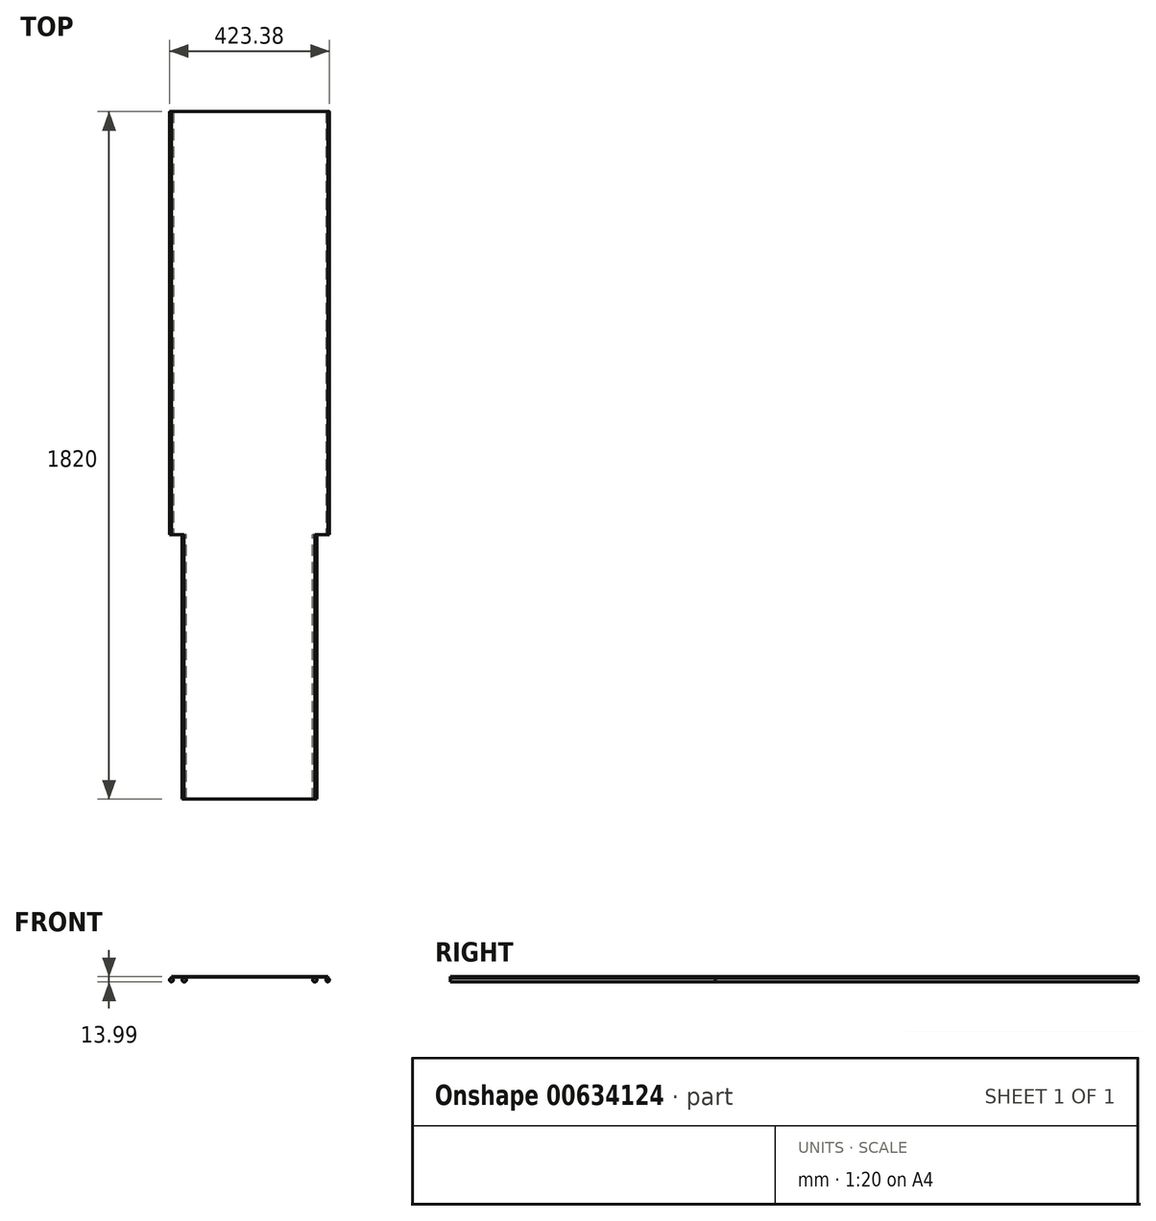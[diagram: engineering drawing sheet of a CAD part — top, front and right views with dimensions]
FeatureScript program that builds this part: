
annotation { "Feature Type Name" : "Feature", "Feature Type Description" : "" }
export const myFeature = defineFeature(function(context is Context, id is Id, definition is map)
    precondition{}
    {
        {
            var Q0;
            Q0=qCreatedBy(makeId("Front.planeOp"),FACE);
            var sketch = newSketch(context, id + "F0", { "sketchPlane" : qUnion([Q0])});
            skLineSegment(sketch, "E0.bottom", {"start": v(-15, 40) * mm, "end": v(15, 40) * mm});
            skLineSegment(sketch, "E0.top", {"start": v(-12, 0) * mm, "end": v(12, 0) * mm});
            skLineSegment(sketch, "E0.left", {"start": v(-15, 40) * mm, "end": v(-15, 37) * mm});
            skLineSegment(sketch, "E0.right", {"start": v(15, 37) * mm, "end": v(15, 3) * mm});
            skLineSegment(sketch, "E1.0", {"start": v(-15, 37) * mm, "end": v(3, 37) * mm});
            skLineSegment(sketch, "E1.1", {"start": v(-12, 6) * mm, "end": v(-12, 6) * mm});
            skLineSegment(sketch, "E1.2", {"start": v(-9, 3) * mm, "end": v(9, 3) * mm});
            skLineSegment(sketch, "E1.3", {"start": v(12, 29.6) * mm, "end": v(12, 6) * mm});
            skLineSegment(sketch, "E2.0", {"start": v(-15, 6) * mm, "end": v(-12, 6) * mm});
            skLineSegment(sketch, "E3", {"start": v(12, 40) * mm, "end": v(7.5, 40) * mm, "construction": true});
            skLineSegment(sketch, "E4", {"start": v(7, 34.8) * mm, "end": v(7, 40) * mm, "construction": true});
            skArc(sketch, "E5", {"start": v(7, 40) * mm, "mid": v(6.75, 29.6) * mm, "end": v(7.5, 39.98) * mm});
            skLineSegment(sketch, "E6.trimOffspring", {"start": v(-15, 6) * mm, "end": v(-15, 3) * mm});
            skPoint(sketch, "E7.orphan", {"position": v(5, 29.7) * mm});
            skPoint(sketch, "E8.visualSharp", {"position": v(15, 40) * mm});
            skArc(sketch, "E8.filletArc", {"start": v(15, 37) * mm, "mid": v(14.12, 39.12) * mm, "end": v(12, 40) * mm});
            skPoint(sketch, "E9.visualSharp", {"position": v(15, 0) * mm});
            skArc(sketch, "E9.filletArc", {"start": v(12, 0) * mm, "mid": v(14.12, 0.88) * mm, "end": v(15, 3) * mm});
            skArc(sketch, "E10.filletArc", {"start": v(9, 3) * mm, "mid": v(11.12, 3.88) * mm, "end": v(12, 6) * mm});
            skPoint(sketch, "E11.visualSharp", {"position": v(-12, 3) * mm});
            skArc(sketch, "E11.filletArc", {"start": v(-12, 6) * mm, "mid": v(-11.12, 3.88) * mm, "end": v(-9, 3) * mm});
            skPoint(sketch, "E12.visualSharp", {"position": v(-15, 0) * mm});
            skArc(sketch, "E12.filletArc", {"start": v(-15, 3) * mm, "mid": v(-14.12, 0.88) * mm, "end": v(-12, 0) * mm});
            skLineSegment(sketch, "E13.0", {"start": v(6.5, 34.8) * mm, "end": v(6.5, 39.8) * mm});
            skLineSegment(sketch, "E14.0", {"start": v(7.5, 34.8) * mm, "end": v(7.5, 40) * mm});
            skLineSegment(sketch, "E15", {"start": v(-15, 6) * mm, "end": v(-15, 16) * mm});
            skLineSegment(sketch, "E16", {"start": v(-15, 16) * mm, "end": v(-12, 16) * mm});
            skLineSegment(sketch, "E17", {"start": v(-12, 16) * mm, "end": v(-12, 6) * mm});
            skLineSegment(sketch, "E18", {"start": v(6.75, 29.6) * mm, "end": v(12, 29.6) * mm});
            skSolve(sketch);
        }
        {
            var Q0;
            Q0=qCreatedBy(makeId("Front.planeOp"),FACE);
            var sketch = newSketch(context, id + "F1", { "sketchPlane" : qUnion([Q0])});
            skLineSegment(sketch, "E19.1.1", {"start": v(7.5, 40) * mm, "end": v(-15, 40) * mm});
            skLineSegment(sketch, "E19.1.2", {"start": v(-15, 40) * mm, "end": v(-15, 37) * mm});
            skArc(sketch, "E19.2.8", {"start": v(-15, 3) * mm, "mid": v(-14.12, 0.88) * mm, "end": v(-12, 0) * mm, "construction": true});
            skLineSegment(sketch, "E19.2.9", {"start": v(-12, 0) * mm, "end": v(-5, 0) * mm});
            skLineSegment(sketch, "E19.2.13", {"start": v(17, 40) * mm, "end": v(8.5, 40) * mm});
            skLineSegment(sketch, "E19.3.0", {"start": v(-15, 18) * mm, "end": v(-15, 7.7) * mm});
            skPoint(sketch, "E20.2", {"position": v(6.5, 37.3) * mm});
            skPoint(sketch, "E21.orphan", {"position": v(6.5, 39.8) * mm});
            skPoint(sketch, "E19.0.2.end.orphan", {"position": v(7, 40) * mm});
            skPoint(sketch, "E22.orphan", {"position": v(12, 29.6) * mm});
            skPoint(sketch, "E23.orphan", {"position": v(7.5, 34.8) * mm});
            skPoint(sketch, "E20.0.start.orphan", {"position": v(6.5, 34.8) * mm});
            skLineSegment(sketch, "E24", {"start": v(-15, 37) * mm, "end": v(-15, 31) * mm});
            skLineSegment(sketch, "E25", {"start": v(0, 0) * mm, "end": v(0, 15) * mm, "construction": true});
            skLineSegment(sketch, "E26", {"start": v(7.5, 40) * mm, "end": v(7.5, 37.97) * mm});
            skLineSegment(sketch, "E27", {"start": v(8.5, 40) * mm, "end": v(8.5, 37.97) * mm});
            skLineSegment(sketch, "E28", {"start": v(15, 32.5) * mm, "end": v(8, 32.5) * mm, "construction": true});
            skPoint(sketch, "E29.orphan", {"position": v(7.6, 39) * mm});
            skLineSegment(sketch, "E30", {"start": v(8, 39) * mm, "end": v(8, 32.5) * mm, "construction": true});
            skPoint(sketch, "E19.3.3.end.orphan", {"position": v(-15, 16) * mm});
            skPoint(sketch, "E19.3.3.start.orphan", {"position": v(-12, 16) * mm});
            skLineSegment(sketch, "E31", {"start": v(-15, 3) * mm, "end": v(-15, 0) * mm});
            skLineSegment(sketch, "E32", {"start": v(-12, 0) * mm, "end": v(-15, 0) * mm});
            skLineSegment(sketch, "E33", {"start": v(-15, 40) * mm, "end": v(-15, 31) * mm, "construction": true});
            skLineSegment(sketch, "E34", {"start": v(-15, 40) * mm, "end": v(-15, 31) * mm});
            skLineSegment(sketch, "E35.trimOffspring", {"start": v(-15, 31) * mm, "end": v(-15, 26) * mm});
            skLineSegment(sketch, "E36.trimOffspring", {"start": v(-15, 29) * mm, "end": v(-15, 24) * mm});
            skPoint(sketch, "E37.orphan", {"position": v(12, 40) * mm});
            skPoint(sketch, "E38.orphan", {"position": v(12, 0) * mm});
            skLineSegment(sketch, "E39.0", {"start": v(13.1, 38) * mm, "end": v(13.1, 38) * mm});
            skLineSegment(sketch, "E40.1", {"start": v(-13, 2) * mm, "end": v(-11, 2) * mm, "construction": true});
            skLineSegment(sketch, "E41.0", {"start": v(-13, 38) * mm, "end": v(-13, 34) * mm});
            skArc(sketch, "E42", {"start": v(13.32, 33.87) * mm, "mid": v(11.56, 36.69) * mm, "end": v(8.5, 37.97) * mm});
            skLineSegment(sketch, "E43.0", {"start": v(29.42, 20) * mm, "end": v(-7, 20) * mm, "construction": true});
            skLineSegment(sketch, "E44.trimOffspring", {"start": v(-13, 0.17) * mm, "end": v(-13, 0) * mm});
            skArc(sketch, "E45.0", {"start": v(2.9, 38) * mm, "mid": v(3.81, 26.3) * mm, "end": v(15, 29.84) * mm});
            skLineSegment(sketch, "E46.trimOffspring", {"start": v(2.9, 38) * mm, "end": v(-13, 38) * mm});
            skLineSegment(sketch, "E47.trimOffspring", {"start": v(13.32, 33.87) * mm, "end": v(13.43, 31.7) * mm});
            skArc(sketch, "E48.trimOffspring", {"start": v(13.1, 38) * mm, "mid": v(13.1, 38) * mm, "end": v(13.1, 38) * mm});
            skArc(sketch, "E49.trimOffspring", {"start": v(7.5, 37.97) * mm, "mid": v(4.01, 28.73) * mm, "end": v(13.43, 31.7) * mm});
            skPoint(sketch, "E50.orphan", {"position": v(7.5, 39) * mm});
            skPoint(sketch, "E51.start.orphan", {"position": v(8.5, 39) * mm});
            skLineSegment(sketch, "E52.0", {"start": v(8, 0) * mm, "end": v(8, 13.5) * mm});
            skLineSegment(sketch, "E53.0", {"start": v(-5, 0) * mm, "end": v(-5, 13.5) * mm});
            skLineSegment(sketch, "E54.0", {"start": v(16.47, 12) * mm, "end": v(14.46, 12) * mm, "construction": true});
            skLineSegment(sketch, "E55.trimOffspring", {"start": v(12.84, 12) * mm, "end": v(10, 12) * mm});
            skLineSegment(sketch, "E56.0", {"start": v(1.5, 0) * mm, "end": v(1.5, 20) * mm, "construction": true});
            skLineSegment(sketch, "E57", {"start": v(1.5, 20) * mm, "end": v(-9.16, 15.5) * mm});
            skLineSegment(sketch, "E58", {"start": v(1.5, 20) * mm, "end": v(10.84, 15.5) * mm});
            skLineSegment(sketch, "E59.0", {"start": v(-9.16, 13.5) * mm, "end": v(-5, 13.5) * mm});
            skLineSegment(sketch, "E60", {"start": v(-9.16, 15.5) * mm, "end": v(-9.16, 13.5) * mm});
            skLineSegment(sketch, "E61", {"start": v(10.84, 15.5) * mm, "end": v(10.84, 13.5) * mm});
            skLineSegment(sketch, "E62.trimOffspring", {"start": v(8, 13.5) * mm, "end": v(10.84, 13.5) * mm});
            skLineSegment(sketch, "E63.trimOffspring", {"start": v(10, 2) * mm, "end": v(15, 2) * mm});
            skLineSegment(sketch, "E64.trimOffspring", {"start": v(8, 0) * mm, "end": v(17, 0) * mm});
            skLineSegment(sketch, "E65.0", {"start": v(10, 2) * mm, "end": v(10, 12) * mm});
            skLineSegment(sketch, "E66.0", {"start": v(1.55, 22.2) * mm, "end": v(-7, 18.58) * mm});
            skLineSegment(sketch, "E66.1", {"start": v(1.55, 22.2) * mm, "end": v(12.84, 16.75) * mm});
            skLineSegment(sketch, "E67.0", {"start": v(-11.16, 16.82) * mm, "end": v(-11.16, 15.5) * mm});
            skLineSegment(sketch, "E68.0", {"start": v(-13, 11.5) * mm, "end": v(-7, 11.5) * mm});
            skLineSegment(sketch, "E69", {"start": v(-11.16, 15.5) * mm, "end": v(-11.16, 13.5) * mm});
            skLineSegment(sketch, "E70.0", {"start": v(12.84, 16.75) * mm, "end": v(12.84, 12) * mm});
            skLineSegment(sketch, "E71.0", {"start": v(-13, 6.7) * mm, "end": v(-7, 6.7) * mm, "construction": true});
            skLineSegment(sketch, "E72.0", {"start": v(-15, 7.7) * mm, "end": v(-13, 7.7) * mm});
            skLineSegment(sketch, "E73.0", {"start": v(-15, 5.7) * mm, "end": v(-11, 5.7) * mm});
            skLineSegment(sketch, "E74.0", {"start": v(-15, 3.7) * mm, "end": v(-13, 3.7) * mm, "construction": true});
            skLineSegment(sketch, "E75.trimOffspring", {"start": v(-15, 5.7) * mm, "end": v(-15, 3) * mm});
            skLineSegment(sketch, "E76.trimOffspring", {"start": v(-13, 3.7) * mm, "end": v(-13, 2) * mm, "construction": true});
            skLineSegment(sketch, "E77.trimOffspring", {"start": v(-11, 5.7) * mm, "end": v(-11, 2) * mm});
            skLineSegment(sketch, "E78.0", {"start": v(-13, 13.5) * mm, "end": v(-11.16, 13.5) * mm});
            skLineSegment(sketch, "E79.trimOffspring", {"start": v(-9.16, 13.5) * mm, "end": v(-7, 13.5) * mm});
            skLineSegment(sketch, "E80.trimOffspring", {"start": v(-13, 11.5) * mm, "end": v(-13, 7.7) * mm});
            skLineSegment(sketch, "E81.0", {"start": v(-7, 11.5) * mm, "end": v(-7, 3.7) * mm});
            skLineSegment(sketch, "E82.trimOffspring", {"start": v(-11, 3.7) * mm, "end": v(-7, 3.7) * mm});
            skLineSegment(sketch, "E83.0", {"start": v(17, 40) * mm, "end": v(17, 0) * mm});
            skPoint(sketch, "E84.orphan", {"position": v(17.1, 0) * mm});
            skLineSegment(sketch, "E85.trimOffspring", {"start": v(15, 29.84) * mm, "end": v(15, 2) * mm});
            skPoint(sketch, "E86.start.orphan", {"position": v(15, 40) * mm});
            skLineSegment(sketch, "E87", {"start": v(-13, 13.5) * mm, "end": v(-13, 18) * mm});
            skLineSegment(sketch, "E88.trimOffspring", {"start": v(-15, 22) * mm, "end": v(-15, 21.16) * mm, "construction": true});
            skLineSegment(sketch, "E89.trimOffspring", {"start": v(-15, 22) * mm, "end": v(-15, 18) * mm});
            skPoint(sketch, "E90.start.orphan", {"position": v(-12, 28) * mm});
            skPoint(sketch, "E91.orphan", {"position": v(-12, 29) * mm});
            skLineSegment(sketch, "E92.0", {"start": v(-9, 26) * mm, "end": v(-11, 26) * mm});
            skLineSegment(sketch, "E93.0", {"start": v(-11, 24) * mm, "end": v(-13, 24) * mm});
            skLineSegment(sketch, "E94", {"start": v(-9, 20) * mm, "end": v(-9, 26) * mm});
            skLineSegment(sketch, "E95.0", {"start": v(-11, 20) * mm, "end": v(-11, 22) * mm});
            skLineSegment(sketch, "E96.trimOffspring", {"start": v(-11, 24) * mm, "end": v(-11, 26) * mm});
            skLineSegment(sketch, "E97.trimOffspring", {"start": v(-13, 28) * mm, "end": v(-13, 34) * mm});
            skLineSegment(sketch, "E98", {"start": v(-15, 22) * mm, "end": v(-11, 22) * mm});
            skLineSegment(sketch, "E99", {"start": v(-13, 24) * mm, "end": v(-15, 24) * mm});
            skLineSegment(sketch, "E100.0", {"start": v(-7, 18.58) * mm, "end": v(-7, 28) * mm});
            skLineSegment(sketch, "E101.0", {"start": v(-13, 18) * mm, "end": v(-8.36, 18) * mm});
            skLineSegment(sketch, "E102.trimOffspring", {"start": v(-8.36, 18) * mm, "end": v(-11.16, 16.82) * mm});
            skLineSegment(sketch, "E103.0", {"start": v(-11, 20) * mm, "end": v(-9, 20) * mm});
            skLineSegment(sketch, "E104.0", {"start": v(-7, 28) * mm, "end": v(-13, 28) * mm});
            skSolve(sketch);
        }
        {
            var Q0;
            Q0=qSketchRegion(id+"F1",true);
            extrude(context, id + "F2", {"entities" : qUnion([Q0]), "oppositeDirection" : true, "depth" : 1910 * mm, "offsetDistance" : 25 * mm});
        }
        {
            var Q0;
            Q0=makeQuery(id+"F1.imprint","IMPRINT",FACE,{"disambiguationData":[TD([[makeQuery(id+"F1.imprint","IMPRINT",EDGE,{"derivedFrom":sQuery(id+"F1.wireOp",EDGE,"E19.1.1")}),1.0]])]});
            var sketch = newSketch(context, id + "F3", { "sketchPlane" : qUnion([Q0])});
            skLineSegment(sketch, "E105.0", {"start": v(-13.5, 18) * mm, "end": v(-13.5, -0.51) * mm});
            skSolve(sketch);
        }
        {
            var Q0;
            Q0=makeQuery(id+"F3.imprint","IMPRINT",FACE,{"disambiguationData":[TD([[makeQuery(id+"F3.imprint","IMPRINT",EDGE,{"derivedFrom":makeQuery(id+"F1.imprint","IMPRINT",EDGE,{"derivedFrom":sQuery(id+"F1.wireOp",EDGE,"E19.1.1")})}),1.0]])]});
            var sketch = newSketch(context, id + "F4", { "sketchPlane" : qUnion([Q0])});
            skLineSegment(sketch, "E106.0", {"start": v(-17, 40) * mm, "end": v(-25.5, 40) * mm});
            skLineSegment(sketch, "E107.0", {"start": v(-49.1, 40) * mm, "end": v(-49.1, 18) * mm});
            skLineSegment(sketch, "E108.0", {"start": v(-17, 40) * mm, "end": v(-17, 18) * mm});
            skPoint(sketch, "E109.orphan", {"position": v(7.5, 40) * mm});
            skLineSegment(sketch, "E110.1", {"start": v(-19, 29.83) * mm, "end": v(-19, 20) * mm});
            skLineSegment(sketch, "E110.3", {"start": v(-47.1, 38) * mm, "end": v(-47.1, 20) * mm});
            skArc(sketch, "E111.0", {"start": v(7.5, 37.97) * mm, "mid": v(4.01, 28.73) * mm, "end": v(13.43, 31.7) * mm, "construction": true});
            skLineSegment(sketch, "E112.0", {"start": v(17, 40) * mm, "end": v(8.5, 40) * mm});
            skLineSegment(sketch, "E113.0", {"start": v(7.5, 40) * mm, "end": v(-15, 40) * mm});
            skLineSegment(sketch, "E114.0", {"start": v(-26.6, 40) * mm, "end": v(-26.6, 37.97) * mm});
            skLineSegment(sketch, "E115.0", {"start": v(-25.5, 40) * mm, "end": v(-25.5, 37.98) * mm});
            skLineSegment(sketch, "E116.0", {"start": v(-7, 18.58) * mm, "end": v(-7, 28) * mm});
            skLineSegment(sketch, "E117", {"start": v(-47.1, 23.29) * mm, "end": v(15, 23.29) * mm, "construction": true});
            skPoint(sketch, "E118.orphan", {"position": v(-7, 23.29) * mm});
            skLineSegment(sketch, "E119", {"start": v(8, 32.5) * mm, "end": v(2.5, 32.5) * mm});
            skLineSegment(sketch, "E120.0", {"start": v(8, 39) * mm, "end": v(8, 32.5) * mm});
            skLineSegment(sketch, "E120.1", {"start": v(17, 40) * mm, "end": v(17, 0) * mm});
            skLineSegment(sketch, "E121.trimOffspring", {"start": v(-17, 32.5) * mm, "end": v(-26, 32.5) * mm, "construction": true});
            skArc(sketch, "E122", {"start": v(-26.6, 37.97) * mm, "mid": v(-25.95, 27.01) * mm, "end": v(-25.5, 37.98) * mm});
            skArc(sketch, "E123.0", {"start": v(-31.1, 38) * mm, "mid": v(-30.2, 26.3) * mm, "end": v(-19, 29.83) * mm});
            skLineSegment(sketch, "E124.trimOffspring", {"start": v(-26.6, 40) * mm, "end": v(-49.1, 40) * mm});
            skLineSegment(sketch, "E125.trimOffspring", {"start": v(-26.6, 27.05) * mm, "end": v(-26.6, 20) * mm, "construction": true});
            skLineSegment(sketch, "E126.trimOffspring", {"start": v(-25.5, 27.04) * mm, "end": v(-25.5, 20) * mm, "construction": true});
            skLineSegment(sketch, "E127.trimOffspring", {"start": v(-31.1, 38) * mm, "end": v(-47.1, 38) * mm});
            skLineSegment(sketch, "E128.0", {"start": v(-49.1, 18) * mm, "end": v(-17, 18) * mm});
            skPoint(sketch, "E129.orphan", {"position": v(-8.36, 18) * mm});
            skPoint(sketch, "E130.orphan", {"position": v(-13, 18) * mm});
            skLineSegment(sketch, "E131.0", {"start": v(-47.1, 20) * mm, "end": v(-19, 20) * mm});
            skSolve(sketch);
        }
        {
            var Q0;
            Q0=makeQuery(id+"F1.imprint","IMPRINT",FACE,{"disambiguationData":[TD([[makeQuery(id+"F1.imprint","IMPRINT",EDGE,{"derivedFrom":sQuery(id+"F1.wireOp",EDGE,"E19.1.1")}),1.0]])]});
            var sketch = newSketch(context, id + "F5", { "sketchPlane" : qUnion([Q0])});
            skArc(sketch, "E132.0", {"start": v(7.5, 37.97) * mm, "mid": v(4.01, 28.73) * mm, "end": v(13.43, 31.7) * mm, "construction": true});
            skArc(sketch, "E132.1", {"start": v(13.32, 33.87) * mm, "mid": v(11.56, 36.69) * mm, "end": v(8.5, 37.97) * mm, "construction": true});
            skLineSegment(sketch, "E132.2", {"start": v(7.5, 40) * mm, "end": v(-15, 40) * mm});
            skArc(sketch, "E132.3", {"start": v(-26.6, 37.97) * mm, "mid": v(-25.95, 27.01) * mm, "end": v(-25.5, 37.98) * mm, "construction": true});
            skLineSegment(sketch, "E133.0", {"start": v(-15, 40) * mm, "end": v(-25.5, 40) * mm});
            skPoint(sketch, "E134.orphan", {"position": v(-26.6, 40) * mm});
            skLineSegment(sketch, "E135.0", {"start": v(7.5, 40) * mm, "end": v(7.5, 37.37) * mm});
            skLineSegment(sketch, "E135.1", {"start": v(8.5, 40) * mm, "end": v(8.5, 37.37) * mm});
            skLineSegment(sketch, "E135.2", {"start": v(-25.5, 40) * mm, "end": v(-25.5, 37.37) * mm});
            skLineSegment(sketch, "E135.3", {"start": v(-26.6, 40) * mm, "end": v(-26.6, 37.36) * mm});
            skPoint(sketch, "E135.4", {"position": v(-25.5, 38.99) * mm});
            skLineSegment(sketch, "E136", {"start": v(-49.1, 40) * mm, "end": v(-198.8, 40) * mm});
            skLineSegment(sketch, "E137.0", {"start": v(8.5, 41) * mm, "end": v(-198.8, 41) * mm});
            skLineSegment(sketch, "E138", {"start": v(8.5, 40) * mm, "end": v(8.5, 41) * mm});
            skLineSegment(sketch, "E139", {"start": v(-198.8, 41) * mm, "end": v(-198.8, 40) * mm, "construction": true});
            skArc(sketch, "E140.0", {"start": v(7.5, 37.37) * mm, "mid": v(4.47, 29.12) * mm, "end": v(12.84, 31.8) * mm});
            skArc(sketch, "E141.0", {"start": v(12.74, 33.72) * mm, "mid": v(11.2, 36.21) * mm, "end": v(8.5, 37.37) * mm});
            skArc(sketch, "E142", {"start": v(12.74, 33.72) * mm, "mid": v(12.88, 32.76) * mm, "end": v(12.84, 31.8) * mm});
            skPoint(sketch, "E143.orphan", {"position": v(7.5, 37.97) * mm});
            skPoint(sketch, "E144.orphan", {"position": v(8.5, 37.97) * mm});
            skArc(sketch, "E145.0", {"start": v(-26.6, 37.36) * mm, "mid": v(-25.95, 27.61) * mm, "end": v(-25.5, 37.37) * mm});
            skPoint(sketch, "E146.orphan", {"position": v(-26.6, 37.97) * mm});
            skPoint(sketch, "E147.orphan", {"position": v(-25.5, 37.98) * mm});
            skLineSegment(sketch, "E148.trimOffspring", {"start": v(-26.6, 40) * mm, "end": v(-49.1, 40) * mm});
            skSolve(sketch);
        }
        {
            var Q0;
            Q0=qCreatedBy(makeId("Front.planeOp"),FACE);
            var sketch = newSketch(context, id + "F6", { "sketchPlane" : qUnion([Q0])});
            skLineSegment(sketch, "E149.3", {"start": v(8.5, 40) * mm, "end": v(8.5, 37.37) * mm});
            skLineSegment(sketch, "E149.4", {"start": v(7.5, 40) * mm, "end": v(7.5, 37.37) * mm});
            skLineSegment(sketch, "E149.5", {"start": v(7.5, 40) * mm, "end": v(-15, 40) * mm});
            skLineSegment(sketch, "E149.6", {"start": v(8.5, 41) * mm, "end": v(-198.8, 41) * mm});
            skLineSegment(sketch, "E149.7", {"start": v(8.5, 40) * mm, "end": v(8.5, 41) * mm});
            skLineSegment(sketch, "E149.8", {"start": v(-25.5, 40) * mm, "end": v(-198.8, 40) * mm});
            skLineSegment(sketch, "E149.9", {"start": v(-198.8, 41) * mm, "end": v(-198.8, 40) * mm});
            skLineSegment(sketch, "E150.0", {"start": v(-15, 40) * mm, "end": v(-25.5, 40) * mm});
            skLineSegment(sketch, "E151.0", {"start": v(8, 32.5) * mm, "end": v(2.5, 32.5) * mm, "construction": true});
            skLineSegment(sketch, "E151.1", {"start": v(8, 39) * mm, "end": v(8, 32.5) * mm, "construction": true});
            skArc(sketch, "E152", {"start": v(7.5, 37.37) * mm, "mid": v(8, 27.62) * mm, "end": v(8.5, 37.37) * mm});
            skPoint(sketch, "E153.orphan", {"position": v(-49.1, 40) * mm});
            skSolve(sketch);
        }
        {
            var Q0;
            Q0 = qSketchRegion(id + "F6", true);
            extrude(context, id + "F7", {"entities" : qUnion([Q0]), "operationType" : NewBodyOperationType.ADD, "oppositeDirection" : true, "depth" : 1120 * mm, "offsetDistance" : 25 * mm});
        }
        {
            var Q0;
            {var subQ7=sQuery(id+"F5.wireOp",EDGE,"E132.2");Q0=makeQuery(id+"F5.imprint","IMPRINT",FACE,{"disambiguationData":[TD([[makeQuery(id+"F5.imprint","IMPRINT",EDGE,{"derivedFrom":subQ7}),1.0]])]});}
            var sketch = newSketch(context, id + "F8", { "sketchPlane" : qUnion([Q0])});
            skLineSegment(sketch, "E154.0.0", {"start": v(-15, 0) * mm, "end": v(-13, 0) * mm});
            skLineSegment(sketch, "E154.0.1", {"start": v(-13, 0) * mm, "end": v(-12, 0) * mm});
            skLineSegment(sketch, "E154.0.2", {"start": v(-12, 0) * mm, "end": v(-5, 0) * mm});
            skLineSegment(sketch, "E154.0.3", {"start": v(-5, 0) * mm, "end": v(-5, 13.5) * mm});
            skLineSegment(sketch, "E154.0.4", {"start": v(-5, 13.5) * mm, "end": v(-7, 13.5) * mm});
            skLineSegment(sketch, "E154.0.5", {"start": v(-7, 13.5) * mm, "end": v(-9.16, 13.5) * mm});
            skLineSegment(sketch, "E154.0.6", {"start": v(-9.16, 13.5) * mm, "end": v(-9.16, 15.5) * mm});
            skLineSegment(sketch, "E154.0.7", {"start": v(-9.16, 15.5) * mm, "end": v(1.5, 20) * mm});
            skLineSegment(sketch, "E154.0.8", {"start": v(1.5, 20) * mm, "end": v(10.84, 15.5) * mm});
            skLineSegment(sketch, "E154.0.9", {"start": v(10.84, 15.5) * mm, "end": v(10.84, 13.5) * mm});
            skLineSegment(sketch, "E154.0.10", {"start": v(10.84, 13.5) * mm, "end": v(8, 13.5) * mm});
            skLineSegment(sketch, "E154.0.11", {"start": v(8, 13.5) * mm, "end": v(8, 0) * mm});
            skLineSegment(sketch, "E154.0.12", {"start": v(8, 0) * mm, "end": v(17, 0) * mm});
            skLineSegment(sketch, "E154.0.13", {"start": v(17, 0) * mm, "end": v(17, 40) * mm});
            skLineSegment(sketch, "E154.0.14", {"start": v(17, 40) * mm, "end": v(8.5, 40) * mm});
            skLineSegment(sketch, "E154.0.15", {"start": v(8.5, 40) * mm, "end": v(8.5, 37.97) * mm});
            skArc(sketch, "E154.0.16", {"start": v(8.5, 37.97) * mm, "mid": v(11.56, 36.69) * mm, "end": v(13.32, 33.87) * mm});
            skLineSegment(sketch, "E154.0.17", {"start": v(13.32, 33.87) * mm, "end": v(13.43, 31.7) * mm});
            skArc(sketch, "E154.0.18", {"start": v(13.43, 31.7) * mm, "mid": v(4.01, 28.73) * mm, "end": v(7.5, 37.97) * mm});
            skLineSegment(sketch, "E154.0.19", {"start": v(7.5, 37.97) * mm, "end": v(7.5, 40) * mm});
            skLineSegment(sketch, "E154.0.20", {"start": v(7.5, 40) * mm, "end": v(-15, 40) * mm});
            skLineSegment(sketch, "E154.0.21", {"start": v(-15, 40) * mm, "end": v(-15, 31) * mm});
            skLineSegment(sketch, "E154.0.22", {"start": v(-15, 31) * mm, "end": v(-15, 29) * mm});
            skLineSegment(sketch, "E154.0.23", {"start": v(-15, 29) * mm, "end": v(-15, 24) * mm});
            skLineSegment(sketch, "E154.0.24", {"start": v(-15, 24) * mm, "end": v(-13, 24) * mm});
            skLineSegment(sketch, "E154.0.25", {"start": v(-13, 24) * mm, "end": v(-11, 24) * mm});
            skLineSegment(sketch, "E154.0.26", {"start": v(-11, 24) * mm, "end": v(-11, 26) * mm});
            skLineSegment(sketch, "E154.0.27", {"start": v(-11, 26) * mm, "end": v(-9, 26) * mm});
            skLineSegment(sketch, "E154.0.28", {"start": v(-9, 26) * mm, "end": v(-9, 20) * mm});
            skLineSegment(sketch, "E154.0.29", {"start": v(-9, 20) * mm, "end": v(-11, 20) * mm});
            skLineSegment(sketch, "E154.0.30", {"start": v(-11, 20) * mm, "end": v(-11, 22) * mm});
            skLineSegment(sketch, "E154.0.31", {"start": v(-11, 22) * mm, "end": v(-15, 22) * mm});
            skLineSegment(sketch, "E154.0.32", {"start": v(-15, 22) * mm, "end": v(-15, 18) * mm});
            skLineSegment(sketch, "E154.0.33", {"start": v(-15, 18) * mm, "end": v(-15, 7.7) * mm});
            skLineSegment(sketch, "E154.0.34", {"start": v(-15, 7.7) * mm, "end": v(-13, 7.7) * mm});
            skLineSegment(sketch, "E154.0.35", {"start": v(-13, 7.7) * mm, "end": v(-13, 11.5) * mm});
            skLineSegment(sketch, "E154.0.36", {"start": v(-13, 11.5) * mm, "end": v(-7, 11.5) * mm});
            skLineSegment(sketch, "E154.0.37", {"start": v(-7, 11.5) * mm, "end": v(-7, 3.7) * mm});
            skLineSegment(sketch, "E154.0.38", {"start": v(-7, 3.7) * mm, "end": v(-11, 3.7) * mm});
            skLineSegment(sketch, "E154.0.39", {"start": v(-11, 3.7) * mm, "end": v(-11, 5.7) * mm});
            skLineSegment(sketch, "E154.0.40", {"start": v(-11, 5.7) * mm, "end": v(-15, 5.7) * mm});
            skLineSegment(sketch, "E154.0.41", {"start": v(-15, 5.7) * mm, "end": v(-15, 3) * mm});
            skLineSegment(sketch, "E154.0.42", {"start": v(-15, 3) * mm, "end": v(-15, 0) * mm});
            skLineSegment(sketch, "E155.0.0", {"start": v(12.84, 16.75) * mm, "end": v(12.84, 12) * mm});
            skLineSegment(sketch, "E155.0.1", {"start": v(12.84, 12) * mm, "end": v(10, 12) * mm});
            skLineSegment(sketch, "E155.0.2", {"start": v(10, 12) * mm, "end": v(10, 2) * mm});
            skLineSegment(sketch, "E155.0.3", {"start": v(10, 2) * mm, "end": v(15, 2) * mm});
            skLineSegment(sketch, "E155.0.4", {"start": v(15, 2) * mm, "end": v(15, 29.84) * mm});
            skArc(sketch, "E155.0.5", {"start": v(15, 29.84) * mm, "mid": v(3.81, 26.3) * mm, "end": v(2.9, 38) * mm});
            skLineSegment(sketch, "E155.0.6", {"start": v(2.9, 38) * mm, "end": v(-13, 38) * mm});
            skLineSegment(sketch, "E155.0.7", {"start": v(-13, 38) * mm, "end": v(-13, 34) * mm});
            skLineSegment(sketch, "E155.0.8", {"start": v(-13, 34) * mm, "end": v(-13, 28) * mm});
            skLineSegment(sketch, "E155.0.9", {"start": v(-13, 28) * mm, "end": v(-7, 28) * mm});
            skLineSegment(sketch, "E155.0.10", {"start": v(-7, 28) * mm, "end": v(-7, 18.58) * mm});
            skLineSegment(sketch, "E155.0.11", {"start": v(-7, 18.58) * mm, "end": v(1.55, 22.2) * mm});
            skLineSegment(sketch, "E155.0.12", {"start": v(1.55, 22.2) * mm, "end": v(12.84, 16.75) * mm});
            skLineSegment(sketch, "E156.0.0", {"start": v(-8.36, 18) * mm, "end": v(-13, 18) * mm});
            skLineSegment(sketch, "E156.0.1", {"start": v(-13, 18) * mm, "end": v(-13, 13.5) * mm});
            skLineSegment(sketch, "E156.0.2", {"start": v(-13, 13.5) * mm, "end": v(-11.16, 13.5) * mm});
            skLineSegment(sketch, "E156.0.3", {"start": v(-11.16, 13.5) * mm, "end": v(-11.16, 15.5) * mm});
            skLineSegment(sketch, "E156.0.4", {"start": v(-11.16, 15.5) * mm, "end": v(-11.16, 16.82) * mm});
            skLineSegment(sketch, "E156.0.5", {"start": v(-11.16, 16.82) * mm, "end": v(-8.36, 18) * mm});
            skSolve(sketch);
        }
        {
            var Q0;
            Q0 = qSketchRegion(id + "F8", true);
            extrude(context, id + "F9", {"entities" : qUnion([Q0]), "operationType" : NewBodyOperationType.REMOVE, "oppositeDirection" : true, "depth" : 2000 * mm, "offsetDistance" : 25 * mm});
        }
        {
            var Q0;
            Q0=makeQuery(id+"F7.boolean.opBoolean","MERGE",FACE,{"derivedFrom":[makeQuery(id+"F2.opExtrude","CAP_FACE",FACE,{"disambiguationData":[OSD([sQuery(id+"F1.wireOp",EDGE,"E19.1.1"),sQuery(id+"F1.wireOp",EDGE,"E19.2.9"),sQuery(id+"F1.wireOp",EDGE,"E19.2.13"),sQuery(id+"F1.wireOp",EDGE,"E19.3.0"),sQuery(id+"F1.wireOp",EDGE,"E26"),sQuery(id+"F1.wireOp",EDGE,"E27"),sQuery(id+"F1.wireOp",EDGE,"E31"),sQuery(id+"F1.wireOp",EDGE,"E32"),sQuery(id+"F1.wireOp",EDGE,"E34"),sQuery(id+"F1.wireOp",EDGE,"E35.trimOffspring"),sQuery(id+"F1.wireOp",EDGE,"E36.trimOffspring"),sQuery(id+"F1.wireOp",EDGE,"E39.0"),sQuery(id+"F1.wireOp",EDGE,"E39.0"),sQuery(id+"F1.wireOp",EDGE,"E41.0"),sQuery(id+"F1.wireOp",EDGE,"E42"),sQuery(id+"F1.wireOp",EDGE,"E45.0"),sQuery(id+"F1.wireOp",EDGE,"E46.trimOffspring"),sQuery(id+"F1.wireOp",EDGE,"E47.trimOffspring"),sQuery(id+"F1.wireOp",EDGE,"E48.trimOffspring"),sQuery(id+"F1.wireOp",EDGE,"E49.trimOffspring"),sQuery(id+"F1.wireOp",EDGE,"E52.0"),sQuery(id+"F1.wireOp",EDGE,"E53.0"),sQuery(id+"F1.wireOp",EDGE,"E55.trimOffspring"),sQuery(id+"F1.wireOp",EDGE,"E57"),sQuery(id+"F1.wireOp",EDGE,"E58"),sQuery(id+"F1.wireOp",EDGE,"E59.0"),sQuery(id+"F1.wireOp",EDGE,"E60"),sQuery(id+"F1.wireOp",EDGE,"E61"),sQuery(id+"F1.wireOp",EDGE,"E62.trimOffspring"),sQuery(id+"F1.wireOp",EDGE,"E63.trimOffspring"),sQuery(id+"F1.wireOp",EDGE,"E64.trimOffspring"),sQuery(id+"F1.wireOp",EDGE,"E65.0"),sQuery(id+"F1.wireOp",EDGE,"E66.0"),sQuery(id+"F1.wireOp",EDGE,"E66.1"),sQuery(id+"F1.wireOp",EDGE,"E67.0"),sQuery(id+"F1.wireOp",EDGE,"E68.0"),sQuery(id+"F1.wireOp",EDGE,"E69"),sQuery(id+"F1.wireOp",EDGE,"E70.0"),sQuery(id+"F1.wireOp",EDGE,"E72.0"),sQuery(id+"F1.wireOp",EDGE,"E73.0"),sQuery(id+"F1.wireOp",EDGE,"E75.trimOffspring"),sQuery(id+"F1.wireOp",EDGE,"E77.trimOffspring"),sQuery(id+"F1.wireOp",EDGE,"E78.0"),sQuery(id+"F1.wireOp",EDGE,"E79.trimOffspring"),sQuery(id+"F1.wireOp",EDGE,"E80.trimOffspring"),sQuery(id+"F1.wireOp",EDGE,"E81.0"),sQuery(id+"F1.wireOp",EDGE,"E82.trimOffspring"),sQuery(id+"F1.wireOp",EDGE,"E83.0"),sQuery(id+"F1.wireOp",EDGE,"E85.trimOffspring"),sQuery(id+"F1.wireOp",EDGE,"E87"),sQuery(id+"F1.wireOp",EDGE,"E89.trimOffspring"),sQuery(id+"F1.wireOp",EDGE,"E92.0"),sQuery(id+"F1.wireOp",EDGE,"E93.0"),sQuery(id+"F1.wireOp",EDGE,"E94"),sQuery(id+"F1.wireOp",EDGE,"E95.0"),sQuery(id+"F1.wireOp",EDGE,"E96.trimOffspring"),sQuery(id+"F1.wireOp",EDGE,"E97.trimOffspring"),sQuery(id+"F1.wireOp",EDGE,"E98"),sQuery(id+"F1.wireOp",EDGE,"E99"),sQuery(id+"F1.wireOp",EDGE,"E100.0"),sQuery(id+"F1.wireOp",EDGE,"E101.0"),sQuery(id+"F1.wireOp",EDGE,"E102.trimOffspring"),sQuery(id+"F1.wireOp",EDGE,"E103.0"),sQuery(id+"F1.wireOp",EDGE,"E104.0")])],"isStart":true}),makeQuery(id+"F7.opExtrude","CAP_FACE",FACE,{"disambiguationData":[OSD([sQuery(id+"F6.wireOp",EDGE,"E149.3"),sQuery(id+"F6.wireOp",EDGE,"E149.4"),sQuery(id+"F6.wireOp",EDGE,"E149.5"),sQuery(id+"F6.wireOp",EDGE,"E149.6"),sQuery(id+"F6.wireOp",EDGE,"E149.7"),sQuery(id+"F6.wireOp",EDGE,"E149.8"),sQuery(id+"F6.wireOp",EDGE,"E149.9"),sQuery(id+"F6.wireOp",EDGE,"E150.0"),sQuery(id+"F6.wireOp",EDGE,"E152")])],"isStart":true})]});
            var sketch = newSketch(context, id + "F10", { "sketchPlane" : qUnion([Q0])});
            skLineSegment(sketch, "E157.0", {"start": v(-26.6, 40) * mm, "end": v(-26.6, 37.97) * mm});
            skLineSegment(sketch, "E157.1", {"start": v(-25.5, 41) * mm, "end": v(-25.5, 37.98) * mm});
            skArc(sketch, "E157.2", {"start": v(-26.6, 37.97) * mm, "mid": v(-25.95, 27.01) * mm, "end": v(-25.5, 37.98) * mm});
            skLineSegment(sketch, "E157.3", {"start": v(-25.5, 41) * mm, "end": v(-198.8, 41) * mm});
            skLineSegment(sketch, "E157.4", {"start": v(-26.6, 40) * mm, "end": v(-49.1, 40) * mm});
            skPoint(sketch, "E158.orphan", {"position": v(-25.5, 40) * mm});
            skPoint(sketch, "E159.orphan", {"position": v(8.5, 41) * mm});
            skLineSegment(sketch, "E160.0", {"start": v(-26.6, 40) * mm, "end": v(-198.8, 40) * mm});
            skPoint(sketch, "E161.orphan", {"position": v(7.5, 40) * mm});
            skLineSegment(sketch, "E162.0", {"start": v(-198.8, 41) * mm, "end": v(-198.8, 40) * mm});
            skSolve(sketch);
        }
        {
            var Q0;
            Q0 = qSketchRegion(id + "F10", true);
            extrude(context, id + "F11", {"entities" : qUnion([Q0]), "operationType" : NewBodyOperationType.ADD, "depth" : 700 * mm, "offsetDistance" : 25 * mm});
        }
        {
            var Q0;
            Q0=makeQuery(id+"F2.opExtrude","SWEPT_BODY",BODY,{"disambiguationData":[OSD([sQuery(id+"F1.wireOp",EDGE,"E19.1.1"),sQuery(id+"F1.wireOp",EDGE,"E19.2.9"),sQuery(id+"F1.wireOp",EDGE,"E19.2.13"),sQuery(id+"F1.wireOp",EDGE,"E19.3.0"),sQuery(id+"F1.wireOp",EDGE,"E26"),sQuery(id+"F1.wireOp",EDGE,"E27"),sQuery(id+"F1.wireOp",EDGE,"E31"),sQuery(id+"F1.wireOp",EDGE,"E32"),sQuery(id+"F1.wireOp",EDGE,"E34"),sQuery(id+"F1.wireOp",EDGE,"E35.trimOffspring"),sQuery(id+"F1.wireOp",EDGE,"E36.trimOffspring"),sQuery(id+"F1.wireOp",EDGE,"E39.0"),sQuery(id+"F1.wireOp",EDGE,"E39.0"),sQuery(id+"F1.wireOp",EDGE,"E41.0"),sQuery(id+"F1.wireOp",EDGE,"E42"),sQuery(id+"F1.wireOp",EDGE,"E45.0"),sQuery(id+"F1.wireOp",EDGE,"E46.trimOffspring"),sQuery(id+"F1.wireOp",EDGE,"E47.trimOffspring"),sQuery(id+"F1.wireOp",EDGE,"E48.trimOffspring"),sQuery(id+"F1.wireOp",EDGE,"E49.trimOffspring"),sQuery(id+"F1.wireOp",EDGE,"E52.0"),sQuery(id+"F1.wireOp",EDGE,"E53.0"),sQuery(id+"F1.wireOp",EDGE,"E55.trimOffspring"),sQuery(id+"F1.wireOp",EDGE,"E57"),sQuery(id+"F1.wireOp",EDGE,"E58"),sQuery(id+"F1.wireOp",EDGE,"E59.0"),sQuery(id+"F1.wireOp",EDGE,"E60"),sQuery(id+"F1.wireOp",EDGE,"E61"),sQuery(id+"F1.wireOp",EDGE,"E62.trimOffspring"),sQuery(id+"F1.wireOp",EDGE,"E63.trimOffspring"),sQuery(id+"F1.wireOp",EDGE,"E64.trimOffspring"),sQuery(id+"F1.wireOp",EDGE,"E65.0"),sQuery(id+"F1.wireOp",EDGE,"E66.0"),sQuery(id+"F1.wireOp",EDGE,"E66.1"),sQuery(id+"F1.wireOp",EDGE,"E67.0"),sQuery(id+"F1.wireOp",EDGE,"E68.0"),sQuery(id+"F1.wireOp",EDGE,"E69"),sQuery(id+"F1.wireOp",EDGE,"E70.0"),sQuery(id+"F1.wireOp",EDGE,"E72.0"),sQuery(id+"F1.wireOp",EDGE,"E73.0"),sQuery(id+"F1.wireOp",EDGE,"E75.trimOffspring"),sQuery(id+"F1.wireOp",EDGE,"E77.trimOffspring"),sQuery(id+"F1.wireOp",EDGE,"E78.0"),sQuery(id+"F1.wireOp",EDGE,"E79.trimOffspring"),sQuery(id+"F1.wireOp",EDGE,"E80.trimOffspring"),sQuery(id+"F1.wireOp",EDGE,"E81.0"),sQuery(id+"F1.wireOp",EDGE,"E82.trimOffspring"),sQuery(id+"F1.wireOp",EDGE,"E83.0"),sQuery(id+"F1.wireOp",EDGE,"E85.trimOffspring"),sQuery(id+"F1.wireOp",EDGE,"E87"),sQuery(id+"F1.wireOp",EDGE,"E89.trimOffspring"),sQuery(id+"F1.wireOp",EDGE,"E92.0"),sQuery(id+"F1.wireOp",EDGE,"E93.0"),sQuery(id+"F1.wireOp",EDGE,"E94"),sQuery(id+"F1.wireOp",EDGE,"E95.0"),sQuery(id+"F1.wireOp",EDGE,"E96.trimOffspring"),sQuery(id+"F1.wireOp",EDGE,"E97.trimOffspring"),sQuery(id+"F1.wireOp",EDGE,"E98"),sQuery(id+"F1.wireOp",EDGE,"E99"),sQuery(id+"F1.wireOp",EDGE,"E100.0"),sQuery(id+"F1.wireOp",EDGE,"E101.0"),sQuery(id+"F1.wireOp",EDGE,"E102.trimOffspring"),sQuery(id+"F1.wireOp",EDGE,"E103.0"),sQuery(id+"F1.wireOp",EDGE,"E104.0")])]});
            var Q1;
            Q1=makeQuery(id+"F11.boolean.opBoolean","MERGE",FACE,{"derivedFrom":[makeQuery(id+"F7.opExtrude","SWEPT_FACE",FACE,{"disambiguationData":[OSD([sQuery(id+"F6.wireOp",EDGE,"E149.9")])]}),makeQuery(id+"F11.opExtrude","SWEPT_FACE",FACE,{"disambiguationData":[OSD([sQuery(id+"F10.wireOp",EDGE,"E162.0")])]})]});
            mirror(context, id + "F12", {"operationType" : NewBodyOperationType.ADD, "entities" : qUnion([Q0]), "mirrorPlane" : qUnion([Q1])});
        }
    });
